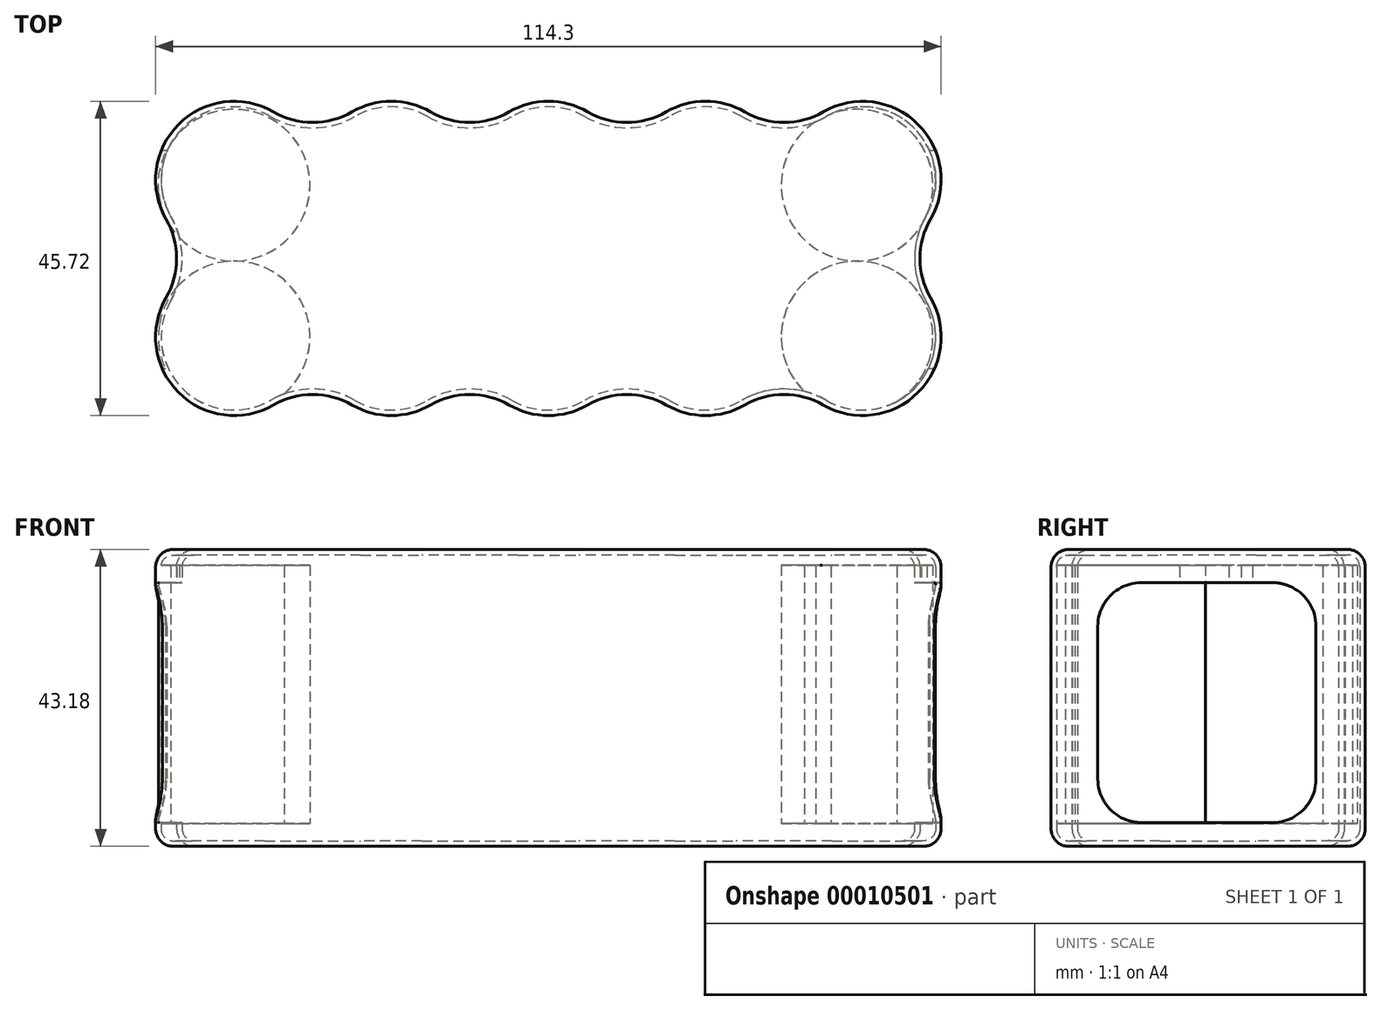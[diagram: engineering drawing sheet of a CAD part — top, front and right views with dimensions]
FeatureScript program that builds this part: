
annotation { "Feature Type Name" : "Feature", "Feature Type Description" : "" }
export const myFeature = defineFeature(function(context is Context, id is Id, definition is map)
    precondition{}
    {
        {
            var Q0;
            Q0=qCreatedBy(makeId("Top.planeOp"),FACE);
            var sketch = newSketch(context, id + "F0", { "sketchPlane" : qUnion([Q0])});
            skArc(sketch, "E0", {"start": v(-9.9, 5.71) * mm, "mid": v(-8.08, -8.08) * mm, "end": v(5.71, -9.9) * mm});
            skArc(sketch, "E1.1.0.0", {"start": v(17.14, -9.9) * mm, "mid": v(22.86, -11.43) * mm, "end": v(28.57, -9.9) * mm});
            skArc(sketch, "E1.2.0.0", {"start": v(40, -9.9) * mm, "mid": v(45.72, -11.43) * mm, "end": v(51.43, -9.9) * mm});
            skArc(sketch, "E1.3.0.0", {"start": v(62.86, -9.9) * mm, "mid": v(68.58, -11.43) * mm, "end": v(74.3, -9.9) * mm});
            skArc(sketch, "E1.4.0.0", {"start": v(85.72, -9.9) * mm, "mid": v(99.52, -8.08) * mm, "end": v(101.34, 5.71) * mm});
            skLineSegment(sketch, "E1.direction1", {"start": v(0, 0) * mm, "end": v(22.86, 0) * mm, "construction": true});
            skArc(sketch, "E2", {"start": v(17.14, -9.9) * mm, "mid": v(11.43, -8.37) * mm, "end": v(5.71, -9.9) * mm});
            skPoint(sketch, "E3.orphan", {"position": v(11.43, 0) * mm});
            skArc(sketch, "E4.1.0.0", {"start": v(40, -9.9) * mm, "mid": v(34.29, -8.37) * mm, "end": v(28.57, -9.9) * mm});
            skArc(sketch, "E4.2.0.0", {"start": v(62.86, -9.9) * mm, "mid": v(57.15, -8.37) * mm, "end": v(51.43, -9.9) * mm});
            skArc(sketch, "E4.3.0.0", {"start": v(85.72, -9.9) * mm, "mid": v(80, -8.37) * mm, "end": v(74.3, -9.9) * mm});
            skLineSegment(sketch, "E5", {"start": v(0, 11.43) * mm, "end": v(91.44, 11.43) * mm, "construction": true});
            skArc(sketch, "E6.0.MirrorCS", {"start": v(17.14, 32.76) * mm, "mid": v(22.86, 34.3) * mm, "end": v(28.57, 32.76) * mm});
            skArc(sketch, "E6.1.MirrorCS", {"start": v(85.72, 32.76) * mm, "mid": v(99.52, 30.94) * mm, "end": v(101.34, 17.15) * mm});
            skPoint(sketch, "E6.2.MirrorP", {"position": v(11.43, 22.86) * mm});
            skArc(sketch, "E6.3.MirrorCS", {"start": v(17.14, 32.76) * mm, "mid": v(11.43, 31.23) * mm, "end": v(5.72, 32.76) * mm});
            skArc(sketch, "E6.4.MirrorCS", {"start": v(62.86, 32.76) * mm, "mid": v(57.15, 31.23) * mm, "end": v(51.43, 32.76) * mm});
            skArc(sketch, "E6.5.MirrorCS", {"start": v(40, 32.76) * mm, "mid": v(45.72, 34.3) * mm, "end": v(51.43, 32.76) * mm});
            skArc(sketch, "E6.6.MirrorCS", {"start": v(62.86, 32.76) * mm, "mid": v(68.58, 34.3) * mm, "end": v(74.3, 32.76) * mm});
            skArc(sketch, "E6.7.MirrorCS", {"start": v(85.72, 32.76) * mm, "mid": v(80, 31.23) * mm, "end": v(74.3, 32.76) * mm});
            skArc(sketch, "E6.8.MirrorCS", {"start": v(40, 32.76) * mm, "mid": v(34.29, 31.23) * mm, "end": v(28.57, 32.76) * mm});
            skArc(sketch, "E6.9.MirrorCS", {"start": v(-9.9, 17.14) * mm, "mid": v(-8.08, 30.94) * mm, "end": v(5.71, 32.76) * mm});
            skArc(sketch, "E7", {"start": v(-9.9, 5.71) * mm, "mid": v(-8.37, 11.43) * mm, "end": v(-9.9, 17.14) * mm});
            skLineSegment(sketch, "E8", {"start": v(45.72, 22.86) * mm, "end": v(45.72, 0) * mm, "construction": true});
            skArc(sketch, "E9.0.MirrorCS", {"start": v(101.34, 5.71) * mm, "mid": v(99.8, 11.43) * mm, "end": v(101.34, 17.15) * mm});
            skSolve(sketch);
        }
        {
            var Q0;
            Q0=qSketchRegion(id+"F0",true);
            extrude(context, id + "F1", {"entities" : qUnion([Q0]), "depth" : 43.18 * mm});
        }
        {
            var Q0;
            Q0=makeQuery(id+"F1.opExtrude","CAP_EDGE",EDGE,{"disambiguationData":[OSD([sQuery(id+"F0.wireOp",EDGE,"E6.6.MirrorCS")])],"isStart":false});
            var Q1;
            Q1=makeQuery(id+"F1.opExtrude","SWEPT_EDGE",EDGE,{"disambiguationData":[OSD([sQuery(id+"F0.wireOp",EDGE,"E6.4.MirrorCS"),sQuery(id+"F0.wireOp",EDGE,"E6.6.MirrorCS")])]});
            var Q2;
            Q2=makeQuery(id+"F1.opExtrude","SWEPT_FACE",FACE,{"disambiguationData":[OSD([sQuery(id+"F0.wireOp",EDGE,"E6.4.MirrorCS")])]});
            var Q3;
            Q3=makeQuery(id+"F1.opExtrude","SWEPT_EDGE",EDGE,{"disambiguationData":[OSD([sQuery(id+"F0.wireOp",EDGE,"E6.5.MirrorCS"),sQuery(id+"F0.wireOp",EDGE,"E6.8.MirrorCS")])]});
            var Q4;
            Q4=makeQuery(id+"F1.opExtrude","SWEPT_FACE",FACE,{"disambiguationData":[OSD([sQuery(id+"F0.wireOp",EDGE,"E9.0.MirrorCS")])]});
            var Q5;
            Q5=makeQuery(id+"F1.opExtrude","CAP_EDGE",EDGE,{"disambiguationData":[OSD([sQuery(id+"F0.wireOp",EDGE,"E6.1.MirrorCS")])],"isStart":true});
            var Q6;
            Q6=makeQuery(id+"F1.opExtrude","CAP_EDGE",EDGE,{"disambiguationData":[OSD([sQuery(id+"F0.wireOp",EDGE,"E1.2.0.0")])],"isStart":true});
            var Q7;
            Q7=makeQuery(id+"F1.opExtrude","SWEPT_FACE",FACE,{"disambiguationData":[OSD([sQuery(id+"F0.wireOp",EDGE,"E0")])]});
            var Q8;
            Q8=makeQuery(id+"F1.opExtrude","SWEPT_FACE",FACE,{"disambiguationData":[OSD([sQuery(id+"F0.wireOp",EDGE,"E6.3.MirrorCS")])]});
            var Q9;
            Q9=makeQuery(id+"F1.opExtrude","SWEPT_EDGE",EDGE,{"disambiguationData":[OSD([sQuery(id+"F0.wireOp",EDGE,"E6.3.MirrorCS"),sQuery(id+"F0.wireOp",EDGE,"E6.9.MirrorCS")])]});
            var Q10;
            Q10=makeQuery(id+"F1.opExtrude","SWEPT_FACE",FACE,{"disambiguationData":[OSD([sQuery(id+"F0.wireOp",EDGE,"E6.5.MirrorCS")])]});
            var Q11;
            Q11=makeQuery(id+"F1.opExtrude","CAP_EDGE",EDGE,{"disambiguationData":[OSD([sQuery(id+"F0.wireOp",EDGE,"E6.7.MirrorCS")])],"isStart":false});
            var Q12;
            Q12=makeQuery(id+"F1.opExtrude","SWEPT_FACE",FACE,{"disambiguationData":[OSD([sQuery(id+"F0.wireOp",EDGE,"E6.7.MirrorCS")])]});
            var Q13;
            Q13=makeQuery(id+"F1.opExtrude","CAP_EDGE",EDGE,{"disambiguationData":[OSD([sQuery(id+"F0.wireOp",EDGE,"E6.3.MirrorCS")])],"isStart":false});
            var Q14;
            Q14=makeQuery(id+"F1.opExtrude","CAP_EDGE",EDGE,{"disambiguationData":[OSD([sQuery(id+"F0.wireOp",EDGE,"E6.5.MirrorCS")])],"isStart":true});
            var Q15;
            Q15=makeQuery(id+"F1.opExtrude","SWEPT_FACE",FACE,{"disambiguationData":[OSD([sQuery(id+"F0.wireOp",EDGE,"E6.9.MirrorCS")])]});
            var Q16;
            Q16=makeQuery(id+"F1.opExtrude","CAP_EDGE",EDGE,{"disambiguationData":[OSD([sQuery(id+"F0.wireOp",EDGE,"E0")])],"isStart":true});
            var Q17;
            Q17=makeQuery(id+"F1.opExtrude","CAP_EDGE",EDGE,{"disambiguationData":[OSD([sQuery(id+"F0.wireOp",EDGE,"E6.8.MirrorCS")])],"isStart":true});
            var Q18;
            Q18=makeQuery(id+"F1.opExtrude","SWEPT_FACE",FACE,{"disambiguationData":[OSD([sQuery(id+"F0.wireOp",EDGE,"E6.1.MirrorCS")])]});
            var Q19;
            Q19=makeQuery(id+"F1.opExtrude","SWEPT_FACE",FACE,{"disambiguationData":[OSD([sQuery(id+"F0.wireOp",EDGE,"E6.0.MirrorCS")])]});
            var Q20;
            Q20=makeQuery(id+"F1.opExtrude","CAP_EDGE",EDGE,{"disambiguationData":[OSD([sQuery(id+"F0.wireOp",EDGE,"E6.1.MirrorCS")])],"isStart":false});
            var Q21;
            Q21=makeQuery(id+"F1.opExtrude","SWEPT_FACE",FACE,{"disambiguationData":[OSD([sQuery(id+"F0.wireOp",EDGE,"E4.3.0.0")])]});
            var Q22;
            Q22=makeQuery(id+"F1.opExtrude","SWEPT_EDGE",EDGE,{"disambiguationData":[OSD([sQuery(id+"F0.wireOp",EDGE,"E6.0.MirrorCS"),sQuery(id+"F0.wireOp",EDGE,"E6.3.MirrorCS")])]});
            var Q23;
            Q23=makeQuery(id+"F1.opExtrude","SWEPT_FACE",FACE,{"disambiguationData":[OSD([sQuery(id+"F0.wireOp",EDGE,"E4.2.0.0")])]});
            var Q24;
            Q24=makeQuery(id+"F1.opExtrude","CAP_EDGE",EDGE,{"disambiguationData":[OSD([sQuery(id+"F0.wireOp",EDGE,"E6.9.MirrorCS")])],"isStart":false});
            var Q25;
            Q25=makeQuery(id+"F1.opExtrude","SWEPT_FACE",FACE,{"disambiguationData":[OSD([sQuery(id+"F0.wireOp",EDGE,"E4.1.0.0")])]});
            var Q26;
            Q26=makeQuery(id+"F1.opExtrude","CAP_EDGE",EDGE,{"disambiguationData":[OSD([sQuery(id+"F0.wireOp",EDGE,"E6.9.MirrorCS")])],"isStart":true});
            var Q27;
            Q27=makeQuery(id+"F1.opExtrude","CAP_EDGE",EDGE,{"disambiguationData":[OSD([sQuery(id+"F0.wireOp",EDGE,"E6.0.MirrorCS")])],"isStart":true});
            var Q28;
            Q28=makeQuery(id+"F1.opExtrude","SWEPT_FACE",FACE,{"disambiguationData":[OSD([sQuery(id+"F0.wireOp",EDGE,"E2")])]});
            var Q29;
            Q29=makeQuery(id+"F1.opExtrude","SWEPT_FACE",FACE,{"disambiguationData":[OSD([sQuery(id+"F0.wireOp",EDGE,"E1.4.0.0")])]});
            var Q30;
            Q30=makeQuery(id+"F1.opExtrude","SWEPT_FACE",FACE,{"disambiguationData":[OSD([sQuery(id+"F0.wireOp",EDGE,"E7")])]});
            var Q31;
            Q31=makeQuery(id+"F1.opExtrude","CAP_FACE",FACE,{"disambiguationData":[OSD([sQuery(id+"F0.wireOp",EDGE,"E0"),sQuery(id+"F0.wireOp",EDGE,"E1.1.0.0"),sQuery(id+"F0.wireOp",EDGE,"E1.2.0.0"),sQuery(id+"F0.wireOp",EDGE,"E1.3.0.0"),sQuery(id+"F0.wireOp",EDGE,"E1.4.0.0"),sQuery(id+"F0.wireOp",EDGE,"E2"),sQuery(id+"F0.wireOp",EDGE,"E4.1.0.0"),sQuery(id+"F0.wireOp",EDGE,"E4.2.0.0"),sQuery(id+"F0.wireOp",EDGE,"E4.3.0.0"),sQuery(id+"F0.wireOp",EDGE,"E6.0.MirrorCS"),sQuery(id+"F0.wireOp",EDGE,"E6.1.MirrorCS"),sQuery(id+"F0.wireOp",EDGE,"E6.3.MirrorCS"),sQuery(id+"F0.wireOp",EDGE,"E6.4.MirrorCS"),sQuery(id+"F0.wireOp",EDGE,"E6.5.MirrorCS"),sQuery(id+"F0.wireOp",EDGE,"E6.6.MirrorCS"),sQuery(id+"F0.wireOp",EDGE,"E6.7.MirrorCS"),sQuery(id+"F0.wireOp",EDGE,"E6.8.MirrorCS"),sQuery(id+"F0.wireOp",EDGE,"E6.9.MirrorCS"),sQuery(id+"F0.wireOp",EDGE,"E7"),sQuery(id+"F0.wireOp",EDGE,"E9.0.MirrorCS")])],"isStart":false});
            var Q32;
            Q32=makeQuery(id+"F1.opExtrude","CAP_FACE",FACE,{"disambiguationData":[OSD([sQuery(id+"F0.wireOp",EDGE,"E0"),sQuery(id+"F0.wireOp",EDGE,"E1.1.0.0"),sQuery(id+"F0.wireOp",EDGE,"E1.2.0.0"),sQuery(id+"F0.wireOp",EDGE,"E1.3.0.0"),sQuery(id+"F0.wireOp",EDGE,"E1.4.0.0"),sQuery(id+"F0.wireOp",EDGE,"E2"),sQuery(id+"F0.wireOp",EDGE,"E4.1.0.0"),sQuery(id+"F0.wireOp",EDGE,"E4.2.0.0"),sQuery(id+"F0.wireOp",EDGE,"E4.3.0.0"),sQuery(id+"F0.wireOp",EDGE,"E6.0.MirrorCS"),sQuery(id+"F0.wireOp",EDGE,"E6.1.MirrorCS"),sQuery(id+"F0.wireOp",EDGE,"E6.3.MirrorCS"),sQuery(id+"F0.wireOp",EDGE,"E6.4.MirrorCS"),sQuery(id+"F0.wireOp",EDGE,"E6.5.MirrorCS"),sQuery(id+"F0.wireOp",EDGE,"E6.6.MirrorCS"),sQuery(id+"F0.wireOp",EDGE,"E6.7.MirrorCS"),sQuery(id+"F0.wireOp",EDGE,"E6.8.MirrorCS"),sQuery(id+"F0.wireOp",EDGE,"E6.9.MirrorCS"),sQuery(id+"F0.wireOp",EDGE,"E7"),sQuery(id+"F0.wireOp",EDGE,"E9.0.MirrorCS")])],"isStart":true});
            var Q33;
            Q33=makeQuery(id+"F1.opExtrude","CAP_EDGE",EDGE,{"disambiguationData":[OSD([sQuery(id+"F0.wireOp",EDGE,"E6.8.MirrorCS")])],"isStart":false});
            var Q34;
            Q34=makeQuery(id+"F1.opExtrude","CAP_EDGE",EDGE,{"disambiguationData":[OSD([sQuery(id+"F0.wireOp",EDGE,"E6.3.MirrorCS")])],"isStart":true});
            var Q35;
            Q35=makeQuery(id+"F1.opExtrude","CAP_EDGE",EDGE,{"disambiguationData":[OSD([sQuery(id+"F0.wireOp",EDGE,"E6.4.MirrorCS")])],"isStart":false});
            var Q36;
            Q36=makeQuery(id+"F1.opExtrude","SWEPT_FACE",FACE,{"disambiguationData":[OSD([sQuery(id+"F0.wireOp",EDGE,"E6.8.MirrorCS")])]});
            var Q37;
            Q37=makeQuery(id+"F1.opExtrude","SWEPT_FACE",FACE,{"disambiguationData":[OSD([sQuery(id+"F0.wireOp",EDGE,"E6.6.MirrorCS")])]});
            var Q38;
            Q38=makeQuery(id+"F1.opExtrude","CAP_EDGE",EDGE,{"disambiguationData":[OSD([sQuery(id+"F0.wireOp",EDGE,"E1.4.0.0")])],"isStart":true});
            var Q39;
            Q39=makeQuery(id+"F1.opExtrude","CAP_EDGE",EDGE,{"disambiguationData":[OSD([sQuery(id+"F0.wireOp",EDGE,"E6.4.MirrorCS")])],"isStart":true});
            var Q40;
            Q40=makeQuery(id+"F1.opExtrude","CAP_EDGE",EDGE,{"disambiguationData":[OSD([sQuery(id+"F0.wireOp",EDGE,"E6.5.MirrorCS")])],"isStart":false});
            var Q41;
            Q41=makeQuery(id+"F1.opExtrude","SWEPT_EDGE",EDGE,{"disambiguationData":[OSD([sQuery(id+"F0.wireOp",EDGE,"E6.6.MirrorCS"),sQuery(id+"F0.wireOp",EDGE,"E6.7.MirrorCS")])]});
            var Q42;
            Q42=makeQuery(id+"F1.opExtrude","CAP_EDGE",EDGE,{"disambiguationData":[OSD([sQuery(id+"F0.wireOp",EDGE,"E6.7.MirrorCS")])],"isStart":true});
            var Q43;
            Q43=makeQuery(id+"F1.opExtrude","CAP_EDGE",EDGE,{"disambiguationData":[OSD([sQuery(id+"F0.wireOp",EDGE,"E6.6.MirrorCS")])],"isStart":true});
            var Q44;
            Q44=makeQuery(id+"F1.opExtrude","SWEPT_EDGE",EDGE,{"disambiguationData":[OSD([sQuery(id+"F0.wireOp",EDGE,"E6.1.MirrorCS"),sQuery(id+"F0.wireOp",EDGE,"E9.0.MirrorCS")])]});
            var Q45;
            Q45=makeQuery(id+"F1.opExtrude","CAP_EDGE",EDGE,{"disambiguationData":[OSD([sQuery(id+"F0.wireOp",EDGE,"E4.1.0.0")])],"isStart":false});
            var Q46;
            Q46=makeQuery(id+"F1.opExtrude","CAP_EDGE",EDGE,{"disambiguationData":[OSD([sQuery(id+"F0.wireOp",EDGE,"E1.3.0.0")])],"isStart":true});
            var Q47;
            Q47=makeQuery(id+"F1.opExtrude","CAP_EDGE",EDGE,{"disambiguationData":[OSD([sQuery(id+"F0.wireOp",EDGE,"E7")])],"isStart":true});
            var Q48;
            Q48=makeQuery(id+"F1.opExtrude","SWEPT_EDGE",EDGE,{"disambiguationData":[OSD([sQuery(id+"F0.wireOp",EDGE,"E0"),sQuery(id+"F0.wireOp",EDGE,"E7")])]});
            var Q49;
            Q49=makeQuery(id+"F1.opExtrude","CAP_EDGE",EDGE,{"disambiguationData":[OSD([sQuery(id+"F0.wireOp",EDGE,"E4.2.0.0")])],"isStart":false});
            var Q50;
            Q50=makeQuery(id+"F1.opExtrude","SWEPT_EDGE",EDGE,{"disambiguationData":[OSD([sQuery(id+"F0.wireOp",EDGE,"E6.9.MirrorCS"),sQuery(id+"F0.wireOp",EDGE,"E7")])]});
            var Q51;
            Q51=makeQuery(id+"F1.opExtrude","CAP_EDGE",EDGE,{"disambiguationData":[OSD([sQuery(id+"F0.wireOp",EDGE,"E9.0.MirrorCS")])],"isStart":false});
            var Q52;
            Q52=makeQuery(id+"F1.opExtrude","CAP_EDGE",EDGE,{"disambiguationData":[OSD([sQuery(id+"F0.wireOp",EDGE,"E1.3.0.0")])],"isStart":false});
            var Q53;
            Q53=makeQuery(id+"F1.opExtrude","CAP_EDGE",EDGE,{"disambiguationData":[OSD([sQuery(id+"F0.wireOp",EDGE,"E2")])],"isStart":true});
            var Q54;
            Q54=makeQuery(id+"F1.opExtrude","CAP_EDGE",EDGE,{"disambiguationData":[OSD([sQuery(id+"F0.wireOp",EDGE,"E4.3.0.0")])],"isStart":true});
            var Q55;
            Q55=makeQuery(id+"F1.opExtrude","SWEPT_EDGE",EDGE,{"disambiguationData":[OSD([sQuery(id+"F0.wireOp",EDGE,"E6.1.MirrorCS"),sQuery(id+"F0.wireOp",EDGE,"E6.7.MirrorCS")])]});
            var Q56;
            Q56=makeQuery(id+"F1.opExtrude","SWEPT_EDGE",EDGE,{"disambiguationData":[OSD([sQuery(id+"F0.wireOp",EDGE,"E6.0.MirrorCS"),sQuery(id+"F0.wireOp",EDGE,"E6.8.MirrorCS")])]});
            var Q57;
            Q57=makeQuery(id+"F1.opExtrude","CAP_EDGE",EDGE,{"disambiguationData":[OSD([sQuery(id+"F0.wireOp",EDGE,"E1.2.0.0")])],"isStart":false});
            var Q58;
            Q58=makeQuery(id+"F1.opExtrude","CAP_EDGE",EDGE,{"disambiguationData":[OSD([sQuery(id+"F0.wireOp",EDGE,"E7")])],"isStart":false});
            var Q59;
            Q59=makeQuery(id+"F1.opExtrude","CAP_EDGE",EDGE,{"disambiguationData":[OSD([sQuery(id+"F0.wireOp",EDGE,"E1.1.0.0")])],"isStart":false});
            var Q60;
            Q60=makeQuery(id+"F1.opExtrude","SWEPT_EDGE",EDGE,{"disambiguationData":[OSD([sQuery(id+"F0.wireOp",EDGE,"E1.4.0.0"),sQuery(id+"F0.wireOp",EDGE,"E9.0.MirrorCS")])]});
            var Q61;
            Q61=makeQuery(id+"F1.opExtrude","SWEPT_EDGE",EDGE,{"disambiguationData":[OSD([sQuery(id+"F0.wireOp",EDGE,"E1.4.0.0"),sQuery(id+"F0.wireOp",EDGE,"E4.3.0.0")])]});
            var Q62;
            Q62=makeQuery(id+"F1.opExtrude","CAP_EDGE",EDGE,{"disambiguationData":[OSD([sQuery(id+"F0.wireOp",EDGE,"E6.0.MirrorCS")])],"isStart":false});
            var Q63;
            Q63=makeQuery(id+"F1.opExtrude","SWEPT_EDGE",EDGE,{"disambiguationData":[OSD([sQuery(id+"F0.wireOp",EDGE,"E1.3.0.0"),sQuery(id+"F0.wireOp",EDGE,"E4.3.0.0")])]});
            var Q64;
            Q64=makeQuery(id+"F1.opExtrude","CAP_EDGE",EDGE,{"disambiguationData":[OSD([sQuery(id+"F0.wireOp",EDGE,"E1.1.0.0")])],"isStart":true});
            var Q65;
            Q65=makeQuery(id+"F1.opExtrude","SWEPT_EDGE",EDGE,{"disambiguationData":[OSD([sQuery(id+"F0.wireOp",EDGE,"E1.3.0.0"),sQuery(id+"F0.wireOp",EDGE,"E4.2.0.0")])]});
            var Q66;
            Q66=makeQuery(id+"F1.opExtrude","SWEPT_FACE",FACE,{"disambiguationData":[OSD([sQuery(id+"F0.wireOp",EDGE,"E1.3.0.0")])]});
            var Q67;
            Q67=makeQuery(id+"F1.opExtrude","SWEPT_FACE",FACE,{"disambiguationData":[OSD([sQuery(id+"F0.wireOp",EDGE,"E1.2.0.0")])]});
            var Q68;
            Q68=makeQuery(id+"F1.opExtrude","SWEPT_EDGE",EDGE,{"disambiguationData":[OSD([sQuery(id+"F0.wireOp",EDGE,"E1.2.0.0"),sQuery(id+"F0.wireOp",EDGE,"E4.1.0.0")])]});
            var Q69;
            Q69=makeQuery(id+"F1.opExtrude","SWEPT_FACE",FACE,{"disambiguationData":[OSD([sQuery(id+"F0.wireOp",EDGE,"E1.1.0.0")])]});
            var Q70;
            Q70=makeQuery(id+"F1.opExtrude","SWEPT_EDGE",EDGE,{"disambiguationData":[OSD([sQuery(id+"F0.wireOp",EDGE,"E1.1.0.0"),sQuery(id+"F0.wireOp",EDGE,"E4.1.0.0")])]});
            var Q71;
            Q71=makeQuery(id+"F1.opExtrude","SWEPT_EDGE",EDGE,{"disambiguationData":[OSD([sQuery(id+"F0.wireOp",EDGE,"E1.1.0.0"),sQuery(id+"F0.wireOp",EDGE,"E2")])]});
            var Q72;
            Q72=makeQuery(id+"F1.opExtrude","SWEPT_EDGE",EDGE,{"disambiguationData":[OSD([sQuery(id+"F0.wireOp",EDGE,"E0"),sQuery(id+"F0.wireOp",EDGE,"E2")])]});
            var Q73;
            Q73=makeQuery(id+"F1.opExtrude","CAP_EDGE",EDGE,{"disambiguationData":[OSD([sQuery(id+"F0.wireOp",EDGE,"E4.3.0.0")])],"isStart":false});
            var Q74;
            Q74=makeQuery(id+"F1.opExtrude","CAP_EDGE",EDGE,{"disambiguationData":[OSD([sQuery(id+"F0.wireOp",EDGE,"E0")])],"isStart":false});
            var Q75;
            Q75=makeQuery(id+"F1.opExtrude","CAP_EDGE",EDGE,{"disambiguationData":[OSD([sQuery(id+"F0.wireOp",EDGE,"E9.0.MirrorCS")])],"isStart":true});
            var Q76;
            Q76=makeQuery(id+"F1.opExtrude","CAP_EDGE",EDGE,{"disambiguationData":[OSD([sQuery(id+"F0.wireOp",EDGE,"E1.4.0.0")])],"isStart":false});
            var Q77;
            Q77=makeQuery(id+"F1.opExtrude","CAP_EDGE",EDGE,{"disambiguationData":[OSD([sQuery(id+"F0.wireOp",EDGE,"E2")])],"isStart":false});
            var Q78;
            Q78=makeQuery(id+"F1.opExtrude","CAP_EDGE",EDGE,{"disambiguationData":[OSD([sQuery(id+"F0.wireOp",EDGE,"E4.2.0.0")])],"isStart":true});
            var Q79;
            Q79=makeQuery(id+"F1.opExtrude","CAP_EDGE",EDGE,{"disambiguationData":[OSD([sQuery(id+"F0.wireOp",EDGE,"E4.1.0.0")])],"isStart":true});
            var Q80;
            Q80=makeQuery(id+"F1.opExtrude","SWEPT_EDGE",EDGE,{"disambiguationData":[OSD([sQuery(id+"F0.wireOp",EDGE,"E6.4.MirrorCS"),sQuery(id+"F0.wireOp",EDGE,"E6.5.MirrorCS")])]});
            var Q81;
            Q81=makeQuery(id+"F1.opExtrude","SWEPT_EDGE",EDGE,{"disambiguationData":[OSD([sQuery(id+"F0.wireOp",EDGE,"E1.2.0.0"),sQuery(id+"F0.wireOp",EDGE,"E4.2.0.0")])]});
            fillet(context, id + "F2", {"entities" : qUnion([Q0, Q1, Q2, Q3, Q4, Q5, Q6, Q7, Q8, Q9, Q10, Q11, Q12, Q13, Q14, Q15, Q16, Q17, Q18, Q19, Q20, Q21, Q22, Q23, Q24, Q25, Q26, Q27, Q28, Q29, Q30, Q31, Q32, Q33, Q34, Q35, Q36, Q37, Q38, Q39, Q40, Q41, Q42, Q43, Q44, Q45, Q46, Q47, Q48, Q49, Q50, Q51, Q52, Q53, Q54, Q55, Q56, Q57, Q58, Q59, Q60, Q61, Q62, Q63, Q64, Q65, Q66, Q67, Q68, Q69, Q70, Q71, Q72, Q73, Q74, Q75, Q76, Q77, Q78, Q79, Q80, Q81]), "radius" : 2.54 * mm, "tangentPropagation" : true, "allowEdgeOverflow" : false});
        }
        {
            var Q0;
            Q0=qCreatedBy(makeId("Right.planeOp"),FACE);
            var sketch = newSketch(context, id + "F3", { "sketchPlane" : qUnion([Q0])});
            skLineSegment(sketch, "E10.bottom", {"start": v(1.73, 3.44) * mm, "end": v(20.78, 3.44) * mm});
            skLineSegment(sketch, "E10.top", {"start": v(1.73, 38.37) * mm, "end": v(20.78, 38.37) * mm});
            skLineSegment(sketch, "E10.left", {"start": v(-4.62, 9.8) * mm, "end": v(-4.62, 32.02) * mm});
            skLineSegment(sketch, "E10.right", {"start": v(27.13, 9.8) * mm, "end": v(27.13, 32.02) * mm});
            skPoint(sketch, "E11.visualSharp", {"position": v(-4.62, 3.44) * mm});
            skArc(sketch, "E11.filletArc", {"start": v(-4.62, 9.8) * mm, "mid": v(-2.76, 5.3) * mm, "end": v(1.73, 3.44) * mm});
            skPoint(sketch, "E12.visualSharp", {"position": v(27.13, 3.44) * mm});
            skArc(sketch, "E12.filletArc", {"start": v(20.78, 3.44) * mm, "mid": v(25.27, 5.3) * mm, "end": v(27.13, 9.8) * mm});
            skPoint(sketch, "E13.visualSharp", {"position": v(27.13, 38.37) * mm});
            skArc(sketch, "E13.filletArc", {"start": v(27.13, 32.02) * mm, "mid": v(25.27, 36.5) * mm, "end": v(20.78, 38.37) * mm});
            skPoint(sketch, "E14.visualSharp", {"position": v(-4.62, 38.37) * mm});
            skArc(sketch, "E14.filletArc", {"start": v(1.73, 38.37) * mm, "mid": v(-2.76, 36.5) * mm, "end": v(-4.62, 32.02) * mm});
            skSolve(sketch);
        }
        {
            var Q0;
            {var subQ0=sQuery(id+"F0.wireOp",EDGE,"E7");Q0=makeQuery(id+"F2.opFillet","BLEND_FACE",FACE,{"disambiguationData":[OSD([subQ0]),TDD([makeQuery(id+"F1.opExtrude","CAP_EDGE",EDGE,{"disambiguationData":[OSD([subQ0])],"isStart":true})])]});}
            var Q1;
            {var subQ0=sQuery(id+"F0.wireOp",EDGE,"E7");Q1=makeQuery(id+"F2.opFillet","BLEND_FACE",FACE,{"disambiguationData":[OSD([subQ0]),TDD([makeQuery(id+"F1.opExtrude","CAP_EDGE",EDGE,{"disambiguationData":[OSD([subQ0])],"isStart":false})])]});}
            var Q2;
            Q2=makeQuery(id+"F1.opExtrude","CAP_FACE",FACE,{"disambiguationData":[OSD([sQuery(id+"F0.wireOp",EDGE,"E0"),sQuery(id+"F0.wireOp",EDGE,"E1.1.0.0"),sQuery(id+"F0.wireOp",EDGE,"E1.2.0.0"),sQuery(id+"F0.wireOp",EDGE,"E1.3.0.0"),sQuery(id+"F0.wireOp",EDGE,"E1.4.0.0"),sQuery(id+"F0.wireOp",EDGE,"E2"),sQuery(id+"F0.wireOp",EDGE,"E4.1.0.0"),sQuery(id+"F0.wireOp",EDGE,"E4.2.0.0"),sQuery(id+"F0.wireOp",EDGE,"E4.3.0.0"),sQuery(id+"F0.wireOp",EDGE,"E6.0.MirrorCS"),sQuery(id+"F0.wireOp",EDGE,"E6.1.MirrorCS"),sQuery(id+"F0.wireOp",EDGE,"E6.3.MirrorCS"),sQuery(id+"F0.wireOp",EDGE,"E6.4.MirrorCS"),sQuery(id+"F0.wireOp",EDGE,"E6.5.MirrorCS"),sQuery(id+"F0.wireOp",EDGE,"E6.6.MirrorCS"),sQuery(id+"F0.wireOp",EDGE,"E6.7.MirrorCS"),sQuery(id+"F0.wireOp",EDGE,"E6.8.MirrorCS"),sQuery(id+"F0.wireOp",EDGE,"E6.9.MirrorCS"),sQuery(id+"F0.wireOp",EDGE,"E7"),sQuery(id+"F0.wireOp",EDGE,"E9.0.MirrorCS")])],"isStart":true});
            var Q3;
            {var subQ0=sQuery(id+"F0.wireOp",EDGE,"E6.9.MirrorCS");Q3=makeQuery(id+"F2.opFillet","BLEND_FACE",FACE,{"disambiguationData":[OSD([subQ0]),TDD([makeQuery(id+"F1.opExtrude","CAP_EDGE",EDGE,{"disambiguationData":[OSD([subQ0])],"isStart":true})])]});}
            var Q4;
            {var subQ0=sQuery(id+"F0.wireOp",EDGE,"E6.9.MirrorCS");Q4=makeQuery(id+"F2.opFillet","BLEND_FACE",FACE,{"disambiguationData":[OSD([subQ0]),TDD([makeQuery(id+"F1.opExtrude","CAP_EDGE",EDGE,{"disambiguationData":[OSD([subQ0])],"isStart":false})])]});}
            var Q5;
            {var subQ0=sQuery(id+"F0.wireOp",EDGE,"E0");Q5=makeQuery(id+"F2.opFillet","BLEND_FACE",FACE,{"disambiguationData":[OSD([subQ0]),TDD([makeQuery(id+"F1.opExtrude","CAP_EDGE",EDGE,{"disambiguationData":[OSD([subQ0])],"isStart":false})])]});}
            var Q6;
            Q6=makeQuery(id+"F1.opExtrude","SWEPT_FACE",FACE,{"disambiguationData":[OSD([sQuery(id+"F0.wireOp",EDGE,"E7")])]});
            var Q7;
            Q7=makeQuery(id+"F1.opExtrude","SWEPT_FACE",FACE,{"disambiguationData":[OSD([sQuery(id+"F0.wireOp",EDGE,"E0")])]});
            var Q8;
            Q8=makeQuery(id+"F1.opExtrude","SWEPT_FACE",FACE,{"disambiguationData":[OSD([sQuery(id+"F0.wireOp",EDGE,"E6.9.MirrorCS")])]});
            var Q9;
            Q9=makeQuery(id+"F1.opExtrude","SWEPT_FACE",FACE,{"disambiguationData":[OSD([sQuery(id+"F0.wireOp",EDGE,"E6.6.MirrorCS")])]});
            var Q10;
            {var subQ0=sQuery(id+"F0.wireOp",EDGE,"E6.8.MirrorCS");Q10=makeQuery(id+"F2.opFillet","BLEND_FACE",FACE,{"disambiguationData":[OSD([subQ0]),TDD([makeQuery(id+"F1.opExtrude","CAP_EDGE",EDGE,{"disambiguationData":[OSD([subQ0])],"isStart":false})])]});}
            var Q11;
            Q11=makeQuery(id+"F1.opExtrude","SWEPT_FACE",FACE,{"disambiguationData":[OSD([sQuery(id+"F0.wireOp",EDGE,"E4.2.0.0")])]});
            var Q12;
            {var subQ0=sQuery(id+"F0.wireOp",EDGE,"E6.7.MirrorCS");Q12=makeQuery(id+"F2.opFillet","BLEND_FACE",FACE,{"disambiguationData":[OSD([subQ0]),TDD([makeQuery(id+"F1.opExtrude","CAP_EDGE",EDGE,{"disambiguationData":[OSD([subQ0])],"isStart":false})])]});}
            var Q13;
            {var subQ0=sQuery(id+"F0.wireOp",EDGE,"E6.1.MirrorCS");Q13=makeQuery(id+"F2.opFillet","BLEND_FACE",FACE,{"disambiguationData":[OSD([subQ0]),TDD([makeQuery(id+"F1.opExtrude","CAP_EDGE",EDGE,{"disambiguationData":[OSD([subQ0])],"isStart":false})])]});}
            var Q14;
            Q14=makeQuery(id+"F1.opExtrude","SWEPT_FACE",FACE,{"disambiguationData":[OSD([sQuery(id+"F0.wireOp",EDGE,"E6.3.MirrorCS")])]});
            var Q15;
            {var subQ0=sQuery(id+"F0.wireOp",EDGE,"E6.6.MirrorCS");Q15=makeQuery(id+"F2.opFillet","BLEND_FACE",FACE,{"disambiguationData":[OSD([subQ0]),TDD([makeQuery(id+"F1.opExtrude","CAP_EDGE",EDGE,{"disambiguationData":[OSD([subQ0])],"isStart":false})])]});}
            var Q16;
            Q16=makeQuery(id+"F1.opExtrude","SWEPT_FACE",FACE,{"disambiguationData":[OSD([sQuery(id+"F0.wireOp",EDGE,"E1.3.0.0")])]});
            var Q17;
            {var subQ0=sQuery(id+"F0.wireOp",EDGE,"E6.7.MirrorCS");Q17=makeQuery(id+"F2.opFillet","BLEND_FACE",FACE,{"disambiguationData":[OSD([subQ0]),TDD([makeQuery(id+"F1.opExtrude","CAP_EDGE",EDGE,{"disambiguationData":[OSD([subQ0])],"isStart":true})])]});}
            var Q18;
            {var subQ0=sQuery(id+"F0.wireOp",EDGE,"E6.6.MirrorCS");Q18=makeQuery(id+"F2.opFillet","BLEND_FACE",FACE,{"disambiguationData":[OSD([subQ0]),TDD([makeQuery(id+"F1.opExtrude","CAP_EDGE",EDGE,{"disambiguationData":[OSD([subQ0])],"isStart":true})])]});}
            var Q19;
            Q19=makeQuery(id+"F1.opExtrude","SWEPT_FACE",FACE,{"disambiguationData":[OSD([sQuery(id+"F0.wireOp",EDGE,"E1.1.0.0")])]});
            var Q20;
            Q20=makeQuery(id+"F1.opExtrude","SWEPT_FACE",FACE,{"disambiguationData":[OSD([sQuery(id+"F0.wireOp",EDGE,"E1.2.0.0")])]});
            var Q21;
            {var subQ0=sQuery(id+"F0.wireOp",EDGE,"E6.4.MirrorCS");Q21=makeQuery(id+"F2.opFillet","BLEND_FACE",FACE,{"disambiguationData":[OSD([subQ0]),TDD([makeQuery(id+"F1.opExtrude","CAP_EDGE",EDGE,{"disambiguationData":[OSD([subQ0])],"isStart":true})])]});}
            var Q22;
            {var subQ0=sQuery(id+"F0.wireOp",EDGE,"E6.1.MirrorCS");Q22=makeQuery(id+"F2.opFillet","BLEND_FACE",FACE,{"disambiguationData":[OSD([subQ0]),TDD([makeQuery(id+"F1.opExtrude","CAP_EDGE",EDGE,{"disambiguationData":[OSD([subQ0])],"isStart":true})])]});}
            var Q23;
            {var subQ0=sQuery(id+"F0.wireOp",EDGE,"E6.3.MirrorCS");Q23=makeQuery(id+"F2.opFillet","BLEND_FACE",FACE,{"disambiguationData":[OSD([subQ0]),TDD([makeQuery(id+"F1.opExtrude","CAP_EDGE",EDGE,{"disambiguationData":[OSD([subQ0])],"isStart":true})])]});}
            var Q24;
            {var subQ0=sQuery(id+"F0.wireOp",EDGE,"E9.0.MirrorCS");Q24=makeQuery(id+"F2.opFillet","BLEND_FACE",FACE,{"disambiguationData":[OSD([subQ0]),TDD([makeQuery(id+"F1.opExtrude","CAP_EDGE",EDGE,{"disambiguationData":[OSD([subQ0])],"isStart":true})])]});}
            var Q25;
            Q25=makeQuery(id+"F1.opExtrude","SWEPT_FACE",FACE,{"disambiguationData":[OSD([sQuery(id+"F0.wireOp",EDGE,"E6.4.MirrorCS")])]});
            var Q26;
            Q26=makeQuery(id+"F1.opExtrude","SWEPT_FACE",FACE,{"disambiguationData":[OSD([sQuery(id+"F0.wireOp",EDGE,"E2")])]});
            var Q27;
            {var subQ0=sQuery(id+"F0.wireOp",EDGE,"E6.5.MirrorCS");Q27=makeQuery(id+"F2.opFillet","BLEND_FACE",FACE,{"disambiguationData":[OSD([subQ0]),TDD([makeQuery(id+"F1.opExtrude","CAP_EDGE",EDGE,{"disambiguationData":[OSD([subQ0])],"isStart":false})])]});}
            var Q28;
            {var subQ0=sQuery(id+"F0.wireOp",EDGE,"E6.8.MirrorCS");Q28=makeQuery(id+"F2.opFillet","BLEND_FACE",FACE,{"disambiguationData":[OSD([subQ0]),TDD([makeQuery(id+"F1.opExtrude","CAP_EDGE",EDGE,{"disambiguationData":[OSD([subQ0])],"isStart":true})])]});}
            var Q29;
            Q29=makeQuery(id+"F1.opExtrude","SWEPT_FACE",FACE,{"disambiguationData":[OSD([sQuery(id+"F0.wireOp",EDGE,"E4.1.0.0")])]});
            var Q30;
            {var subQ0=sQuery(id+"F0.wireOp",EDGE,"E4.3.0.0");Q30=makeQuery(id+"F2.opFillet","BLEND_FACE",FACE,{"disambiguationData":[OSD([subQ0]),TDD([makeQuery(id+"F1.opExtrude","CAP_EDGE",EDGE,{"disambiguationData":[OSD([subQ0])],"isStart":true})])]});}
            var Q31;
            Q31=makeQuery(id+"F1.opExtrude","SWEPT_FACE",FACE,{"disambiguationData":[OSD([sQuery(id+"F0.wireOp",EDGE,"E6.7.MirrorCS")])]});
            var Q32;
            {var subQ0=sQuery(id+"F0.wireOp",EDGE,"E6.4.MirrorCS");Q32=makeQuery(id+"F2.opFillet","BLEND_FACE",FACE,{"disambiguationData":[OSD([subQ0]),TDD([makeQuery(id+"F1.opExtrude","CAP_EDGE",EDGE,{"disambiguationData":[OSD([subQ0])],"isStart":false})])]});}
            var Q33;
            Q33=makeQuery(id+"F1.opExtrude","SWEPT_FACE",FACE,{"disambiguationData":[OSD([sQuery(id+"F0.wireOp",EDGE,"E4.3.0.0")])]});
            var Q34;
            {var subQ0=sQuery(id+"F0.wireOp",EDGE,"E6.0.MirrorCS");Q34=makeQuery(id+"F2.opFillet","BLEND_FACE",FACE,{"disambiguationData":[OSD([subQ0]),TDD([makeQuery(id+"F1.opExtrude","CAP_EDGE",EDGE,{"disambiguationData":[OSD([subQ0])],"isStart":true})])]});}
            var Q35;
            {var subQ0=sQuery(id+"F0.wireOp",EDGE,"E4.1.0.0");Q35=makeQuery(id+"F2.opFillet","BLEND_FACE",FACE,{"disambiguationData":[OSD([subQ0]),TDD([makeQuery(id+"F1.opExtrude","CAP_EDGE",EDGE,{"disambiguationData":[OSD([subQ0])],"isStart":true})])]});}
            var Q36;
            {var subQ0=sQuery(id+"F0.wireOp",EDGE,"E2");Q36=makeQuery(id+"F2.opFillet","BLEND_FACE",FACE,{"disambiguationData":[OSD([subQ0]),TDD([makeQuery(id+"F1.opExtrude","CAP_EDGE",EDGE,{"disambiguationData":[OSD([subQ0])],"isStart":false})])]});}
            var Q37;
            {var subQ0=sQuery(id+"F0.wireOp",EDGE,"E6.5.MirrorCS");Q37=makeQuery(id+"F2.opFillet","BLEND_FACE",FACE,{"disambiguationData":[OSD([subQ0]),TDD([makeQuery(id+"F1.opExtrude","CAP_EDGE",EDGE,{"disambiguationData":[OSD([subQ0])],"isStart":true})])]});}
            var Q38;
            {var subQ0=sQuery(id+"F0.wireOp",EDGE,"E2");Q38=makeQuery(id+"F2.opFillet","BLEND_FACE",FACE,{"disambiguationData":[OSD([subQ0]),TDD([makeQuery(id+"F1.opExtrude","CAP_EDGE",EDGE,{"disambiguationData":[OSD([subQ0])],"isStart":true})])]});}
            var Q39;
            {var subQ0=sQuery(id+"F0.wireOp",EDGE,"E1.4.0.0");Q39=makeQuery(id+"F2.opFillet","BLEND_FACE",FACE,{"disambiguationData":[OSD([subQ0]),TDD([makeQuery(id+"F1.opExtrude","CAP_EDGE",EDGE,{"disambiguationData":[OSD([subQ0])],"isStart":false})])]});}
            var Q40;
            Q40=makeQuery(id+"F1.opExtrude","CAP_FACE",FACE,{"disambiguationData":[OSD([sQuery(id+"F0.wireOp",EDGE,"E0"),sQuery(id+"F0.wireOp",EDGE,"E1.1.0.0"),sQuery(id+"F0.wireOp",EDGE,"E1.2.0.0"),sQuery(id+"F0.wireOp",EDGE,"E1.3.0.0"),sQuery(id+"F0.wireOp",EDGE,"E1.4.0.0"),sQuery(id+"F0.wireOp",EDGE,"E2"),sQuery(id+"F0.wireOp",EDGE,"E4.1.0.0"),sQuery(id+"F0.wireOp",EDGE,"E4.2.0.0"),sQuery(id+"F0.wireOp",EDGE,"E4.3.0.0"),sQuery(id+"F0.wireOp",EDGE,"E6.0.MirrorCS"),sQuery(id+"F0.wireOp",EDGE,"E6.1.MirrorCS"),sQuery(id+"F0.wireOp",EDGE,"E6.3.MirrorCS"),sQuery(id+"F0.wireOp",EDGE,"E6.4.MirrorCS"),sQuery(id+"F0.wireOp",EDGE,"E6.5.MirrorCS"),sQuery(id+"F0.wireOp",EDGE,"E6.6.MirrorCS"),sQuery(id+"F0.wireOp",EDGE,"E6.7.MirrorCS"),sQuery(id+"F0.wireOp",EDGE,"E6.8.MirrorCS"),sQuery(id+"F0.wireOp",EDGE,"E6.9.MirrorCS"),sQuery(id+"F0.wireOp",EDGE,"E7"),sQuery(id+"F0.wireOp",EDGE,"E9.0.MirrorCS")])],"isStart":false});
            var Q41;
            {var subQ0=sQuery(id+"F0.wireOp",EDGE,"E1.4.0.0");Q41=makeQuery(id+"F2.opFillet","BLEND_FACE",FACE,{"disambiguationData":[OSD([subQ0]),TDD([makeQuery(id+"F1.opExtrude","CAP_EDGE",EDGE,{"disambiguationData":[OSD([subQ0])],"isStart":true})])]});}
            var Q42;
            Q42=makeQuery(id+"F1.opExtrude","SWEPT_FACE",FACE,{"disambiguationData":[OSD([sQuery(id+"F0.wireOp",EDGE,"E6.8.MirrorCS")])]});
            var Q43;
            {var subQ0=sQuery(id+"F0.wireOp",EDGE,"E1.3.0.0");Q43=makeQuery(id+"F2.opFillet","BLEND_FACE",FACE,{"disambiguationData":[OSD([subQ0]),TDD([makeQuery(id+"F1.opExtrude","CAP_EDGE",EDGE,{"disambiguationData":[OSD([subQ0])],"isStart":true})])]});}
            var Q44;
            Q44=makeQuery(id+"F1.opExtrude","SWEPT_FACE",FACE,{"disambiguationData":[OSD([sQuery(id+"F0.wireOp",EDGE,"E6.0.MirrorCS")])]});
            var Q45;
            {var subQ0=sQuery(id+"F0.wireOp",EDGE,"E6.0.MirrorCS");Q45=makeQuery(id+"F2.opFillet","BLEND_FACE",FACE,{"disambiguationData":[OSD([subQ0]),TDD([makeQuery(id+"F1.opExtrude","CAP_EDGE",EDGE,{"disambiguationData":[OSD([subQ0])],"isStart":false})])]});}
            var Q46;
            {var subQ0=sQuery(id+"F0.wireOp",EDGE,"E4.2.0.0");Q46=makeQuery(id+"F2.opFillet","BLEND_FACE",FACE,{"disambiguationData":[OSD([subQ0]),TDD([makeQuery(id+"F1.opExtrude","CAP_EDGE",EDGE,{"disambiguationData":[OSD([subQ0])],"isStart":true})])]});}
            var Q47;
            {var subQ0=sQuery(id+"F0.wireOp",EDGE,"E0");Q47=makeQuery(id+"F2.opFillet","BLEND_FACE",FACE,{"disambiguationData":[OSD([subQ0]),TDD([makeQuery(id+"F1.opExtrude","CAP_EDGE",EDGE,{"disambiguationData":[OSD([subQ0])],"isStart":true})])]});}
            var Q48;
            {var subQ0=sQuery(id+"F0.wireOp",EDGE,"E1.1.0.0");Q48=makeQuery(id+"F2.opFillet","BLEND_FACE",FACE,{"disambiguationData":[OSD([subQ0]),TDD([makeQuery(id+"F1.opExtrude","CAP_EDGE",EDGE,{"disambiguationData":[OSD([subQ0])],"isStart":true})])]});}
            var Q49;
            {var subQ0=sQuery(id+"F0.wireOp",EDGE,"E1.1.0.0");Q49=makeQuery(id+"F2.opFillet","BLEND_FACE",FACE,{"disambiguationData":[OSD([subQ0]),TDD([makeQuery(id+"F1.opExtrude","CAP_EDGE",EDGE,{"disambiguationData":[OSD([subQ0])],"isStart":false})])]});}
            var Q50;
            {var subQ0=sQuery(id+"F0.wireOp",EDGE,"E1.2.0.0");Q50=makeQuery(id+"F2.opFillet","BLEND_FACE",FACE,{"disambiguationData":[OSD([subQ0]),TDD([makeQuery(id+"F1.opExtrude","CAP_EDGE",EDGE,{"disambiguationData":[OSD([subQ0])],"isStart":true})])]});}
            var Q51;
            Q51=makeQuery(id+"F1.opExtrude","SWEPT_FACE",FACE,{"disambiguationData":[OSD([sQuery(id+"F0.wireOp",EDGE,"E6.5.MirrorCS")])]});
            var Q52;
            {var subQ0=sQuery(id+"F0.wireOp",EDGE,"E6.3.MirrorCS");Q52=makeQuery(id+"F2.opFillet","BLEND_FACE",FACE,{"disambiguationData":[OSD([subQ0]),TDD([makeQuery(id+"F1.opExtrude","CAP_EDGE",EDGE,{"disambiguationData":[OSD([subQ0])],"isStart":false})])]});}
            var Q53;
            Q53=makeQuery(id+"F1.opExtrude","SWEPT_FACE",FACE,{"disambiguationData":[OSD([sQuery(id+"F0.wireOp",EDGE,"E6.1.MirrorCS")])]});
            var Q54;
            Q54=makeQuery(id+"F1.opExtrude","SWEPT_FACE",FACE,{"disambiguationData":[OSD([sQuery(id+"F0.wireOp",EDGE,"E9.0.MirrorCS")])]});
            var Q55;
            Q55=makeQuery(id+"F1.opExtrude","SWEPT_FACE",FACE,{"disambiguationData":[OSD([sQuery(id+"F0.wireOp",EDGE,"E1.4.0.0")])]});
            var Q56;
            {var subQ0=sQuery(id+"F0.wireOp",EDGE,"E4.3.0.0");Q56=makeQuery(id+"F2.opFillet","BLEND_FACE",FACE,{"disambiguationData":[OSD([subQ0]),TDD([makeQuery(id+"F1.opExtrude","CAP_EDGE",EDGE,{"disambiguationData":[OSD([subQ0])],"isStart":false})])]});}
            var Q57;
            {var subQ0=sQuery(id+"F0.wireOp",EDGE,"E1.3.0.0");Q57=makeQuery(id+"F2.opFillet","BLEND_FACE",FACE,{"disambiguationData":[OSD([subQ0]),TDD([makeQuery(id+"F1.opExtrude","CAP_EDGE",EDGE,{"disambiguationData":[OSD([subQ0])],"isStart":false})])]});}
            var Q58;
            {var subQ0=sQuery(id+"F0.wireOp",EDGE,"E4.2.0.0");Q58=makeQuery(id+"F2.opFillet","BLEND_FACE",FACE,{"disambiguationData":[OSD([subQ0]),TDD([makeQuery(id+"F1.opExtrude","CAP_EDGE",EDGE,{"disambiguationData":[OSD([subQ0])],"isStart":false})])]});}
            var Q59;
            {var subQ0=sQuery(id+"F0.wireOp",EDGE,"E4.1.0.0");Q59=makeQuery(id+"F2.opFillet","BLEND_FACE",FACE,{"disambiguationData":[OSD([subQ0]),TDD([makeQuery(id+"F1.opExtrude","CAP_EDGE",EDGE,{"disambiguationData":[OSD([subQ0])],"isStart":false})])]});}
            var Q60;
            {var subQ0=sQuery(id+"F0.wireOp",EDGE,"E1.2.0.0");Q60=makeQuery(id+"F2.opFillet","BLEND_FACE",FACE,{"disambiguationData":[OSD([subQ0]),TDD([makeQuery(id+"F1.opExtrude","CAP_EDGE",EDGE,{"disambiguationData":[OSD([subQ0])],"isStart":false})])]});}
            var Q61;
            {var subQ0=sQuery(id+"F0.wireOp",EDGE,"E9.0.MirrorCS");Q61=makeQuery(id+"F2.opFillet","BLEND_FACE",FACE,{"disambiguationData":[OSD([subQ0]),TDD([makeQuery(id+"F1.opExtrude","CAP_EDGE",EDGE,{"disambiguationData":[OSD([subQ0])],"isStart":false})])]});}
            var Q62;
            Q62=makeQuery(id+"F1.opExtrude","SWEPT_BODY",BODY,{"disambiguationData":[OSD([sQuery(id+"F0.wireOp",EDGE,"E0"),sQuery(id+"F0.wireOp",EDGE,"E1.1.0.0"),sQuery(id+"F0.wireOp",EDGE,"E1.2.0.0"),sQuery(id+"F0.wireOp",EDGE,"E1.3.0.0"),sQuery(id+"F0.wireOp",EDGE,"E1.4.0.0"),sQuery(id+"F0.wireOp",EDGE,"E2"),sQuery(id+"F0.wireOp",EDGE,"E4.1.0.0"),sQuery(id+"F0.wireOp",EDGE,"E4.2.0.0"),sQuery(id+"F0.wireOp",EDGE,"E4.3.0.0"),sQuery(id+"F0.wireOp",EDGE,"E6.0.MirrorCS"),sQuery(id+"F0.wireOp",EDGE,"E6.1.MirrorCS"),sQuery(id+"F0.wireOp",EDGE,"E6.3.MirrorCS"),sQuery(id+"F0.wireOp",EDGE,"E6.4.MirrorCS"),sQuery(id+"F0.wireOp",EDGE,"E6.5.MirrorCS"),sQuery(id+"F0.wireOp",EDGE,"E6.6.MirrorCS"),sQuery(id+"F0.wireOp",EDGE,"E6.7.MirrorCS"),sQuery(id+"F0.wireOp",EDGE,"E6.8.MirrorCS"),sQuery(id+"F0.wireOp",EDGE,"E6.9.MirrorCS"),sQuery(id+"F0.wireOp",EDGE,"E7"),sQuery(id+"F0.wireOp",EDGE,"E9.0.MirrorCS")])]});
            shell(context, id + "F4", {"isHollow" : true, "entities" : qUnion([Q0, Q1, Q2, Q3, Q4, Q5, Q6, Q7, Q8, Q9, Q10, Q11, Q12, Q13, Q14, Q15, Q16, Q17, Q18, Q19, Q20, Q21, Q22, Q23, Q24, Q25, Q26, Q27, Q28, Q29, Q30, Q31, Q32, Q33, Q34, Q35, Q36, Q37, Q38, Q39, Q40, Q41, Q42, Q43, Q44, Q45, Q46, Q47, Q48, Q49, Q50, Q51, Q52, Q53, Q54, Q55, Q56, Q57, Q58, Q59, Q60, Q61]), "parts" : qUnion([Q62]), "thickness" : 0.8 * mm});
        }
        {
            var Q0;
            Q0=qSketchRegion(id+"F3",true);
            extrude(context, id + "F5", {"entities" : qUnion([Q0]), "operationType" : NewBodyOperationType.REMOVE, "endBound" : BoundingType.THROUGH_ALL, "depth" : 25.4 * mm, "hasSecondDirection" : true, "secondDirectionBound" : BoundingType.THROUGH_ALL, "secondDirectionOppositeDirection" : true, "secondDirectionDepth" : 25.4 * mm});
        }
        {
            var Q0;
            Q0=qCreatedBy(makeId("Top.planeOp"),FACE);
            cPlane(context, id + "F6", {"entities" : qUnion([Q0]), "cplaneType" : CPlaneType.OFFSET, "offset" : 3.3 * mm, "width" : 152.4 * mm, "height" : 152.4 * mm});
        }
        {
            var Q0;
            Q0=qCreatedBy(id+"F6.planeOp",FACE);
            var sketch = newSketch(context, id + "F7", { "sketchPlane" : qUnion([Q0])});
            skCircle(sketch, "E15", {"center": v(0, 0) * mm, "radius": 11.03 * mm});
            skLineSegment(sketch, "E16", {"start": v(0, 11.03) * mm, "end": v(59.07, 11.03) * mm, "construction": true});
            skCircle(sketch, "E17.0.1.0", {"center": v(0, 22.1) * mm, "radius": 11.03 * mm});
            skCircle(sketch, "E17.1.0.0", {"center": v(90.65, 0) * mm, "radius": 11.03 * mm});
            skCircle(sketch, "E17.1.1.0", {"center": v(90.65, 22.1) * mm, "radius": 11.03 * mm});
            skLineSegment(sketch, "E17.direction1", {"start": v(0, 0) * mm, "end": v(90.65, 0) * mm, "construction": true});
            skLineSegment(sketch, "E17.direction2", {"start": v(0, 0) * mm, "end": v(0, 22.1) * mm, "construction": true});
            skSolve(sketch);
        }
        {
            var Q0;
            Q0=qSketchRegion(id+"F7",true);
            extrude(context, id + "F8", {"entities" : qUnion([Q0]), "operationType" : NewBodyOperationType.ADD, "depth" : 37.6 * mm});
        }
    });
